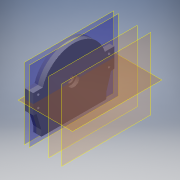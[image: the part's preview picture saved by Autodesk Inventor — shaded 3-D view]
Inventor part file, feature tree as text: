
AUTODESK INVENTOR PART (.ipt)
format: ipt  version: 2019 (Build 230136000, 136)  size: 496,640 bytes
history: native  units: mm
features: sketch x26, extrude x21, mirror x13, plane x12, projected_geometry x11, fillet x4, hole x3, other x2
ambient origin geometry x8: Origin, YZ Plane, XZ Plane, XY Plane, X Axis, Y Axis, Z Axis, Center Point
bodies: Body1 (feature_tree)
feature tree (92):
  other  "實體1"
  extrude  "擠出1"  Depth=123.43mm
  plane  "工作平面2"
  extrude  "擠出3"  Depth=160.0mm
  plane  "工作平面3"
  extrude  "擠出4"  Depth=120.0mm TaperAngle=0.0deg
  extrude  "擠出5"  [1 undecoded]
  plane  "工作平面4"
  extrude  "擠出7"  Depth=130.0mm
  plane  "工作平面5"
  extrude  "擠出9"  Depth=15.0mm TaperAngle=0.0deg
  extrude  "擠出10"  [1 undecoded]
  extrude  "擠出11"  Depth=140.0mm
  extrude  "擠出12"  Depth=10.0mm TaperAngle=0.0deg
  mirror  "鏡射1"
  fillet  "圓角2"  Radius=10.0mm
  fillet  "圓角3"  Radius=10.0mm
  sketch  "草圖16"
  plane  "工作平面7"
  mirror  "鏡射2"
  fillet  "圓角5"  [1 undecoded]
  fillet  "圓角6"  Radius=10.0mm
  plane  "工作平面8"
  plane  "工作平面9"
  sketch  "草圖20"
  extrude  "擠出15"  [1 undecoded]
  plane  "工作平面10"
  extrude  "擠出16"  Depth=10.0mm
  extrude  "擠出17"  Depth=10.0mm TaperAngle=0.0deg
  plane  "工作平面11"
  extrude  "擠出19"  Depth=10.0mm TaperAngle=0.0deg
  extrude  "擠出20"  Depth=160.0mm
  mirror  "鏡射3"
  mirror  "鏡射4"
  extrude  "擠出21"  Depth=80.0mm
  mirror  "鏡射7"
  plane  "工作平面15"
  mirror  "鏡射9"
  hole  "孔2"  [1 undecoded]
  mirror  "鏡射10"
  mirror  "鏡射11"
  hole  "孔3"  [1 undecoded]
  mirror  "鏡射12"
  mirror  "鏡射13"
  extrude  "擠出22"  Depth=160.0mm
  extrude  "擠出23"  Depth=120.0mm TaperAngle=0.0deg
  extrude  "擠出24"  Depth=120.0mm TaperAngle=0.0deg
  extrude  "擠出25"  Depth=25.0mm
  extrude  "擠出27"  Depth=20.0mm
  extrude  "擠出28"  Depth=2.0mm
  mirror  "鏡射14"
  plane  "工作平面17"
  hole  "孔4"  [1 undecoded]
  mirror  "鏡射15"
  mirror  "鏡射16"
  other  "分割1"
  sketch  "草圖1"
  sketch  "草圖4"
  sketch  "草圖6"
  sketch  "草圖7"
  projected_geometry  "投影迴路1"
  sketch  "草圖9"
  projected_geometry  "投影迴路4"
  sketch  "草圖11"
  sketch  "草圖12"
  projected_geometry  "投影迴路6"
  sketch  "草圖13"
  projected_geometry  "投影迴路7"
  sketch  "草圖14"
  plane  "工作平面6"
  sketch  "草圖17"
  projected_geometry  "投影迴路8"
  sketch  "草圖24"
  projected_geometry  "投影迴路11"
  sketch  "草圖25"
  sketch  "草圖26"
  sketch  "草圖27"
  sketch  "草圖28"
  sketch  "草圖29"
  projected_geometry  "投影迴路12"
  sketch  "草圖30"
  sketch  "草圖31"
  sketch  "草圖32"
  projected_geometry  "投影迴路13"
  projected_geometry  "投影迴路14"
  projected_geometry  "投影迴路15"
  sketch  "草圖33"
  sketch  "草圖34"
  sketch  "草圖35"
  projected_geometry  "投影迴路16"
  sketch  "草圖36"
  sketch  "草圖37"
note: 7 required parameter values undecoded (feature->parameter linkage not recoverable at this tier; creation-order binding heuristic only, values carry confidence <= 0.55)
